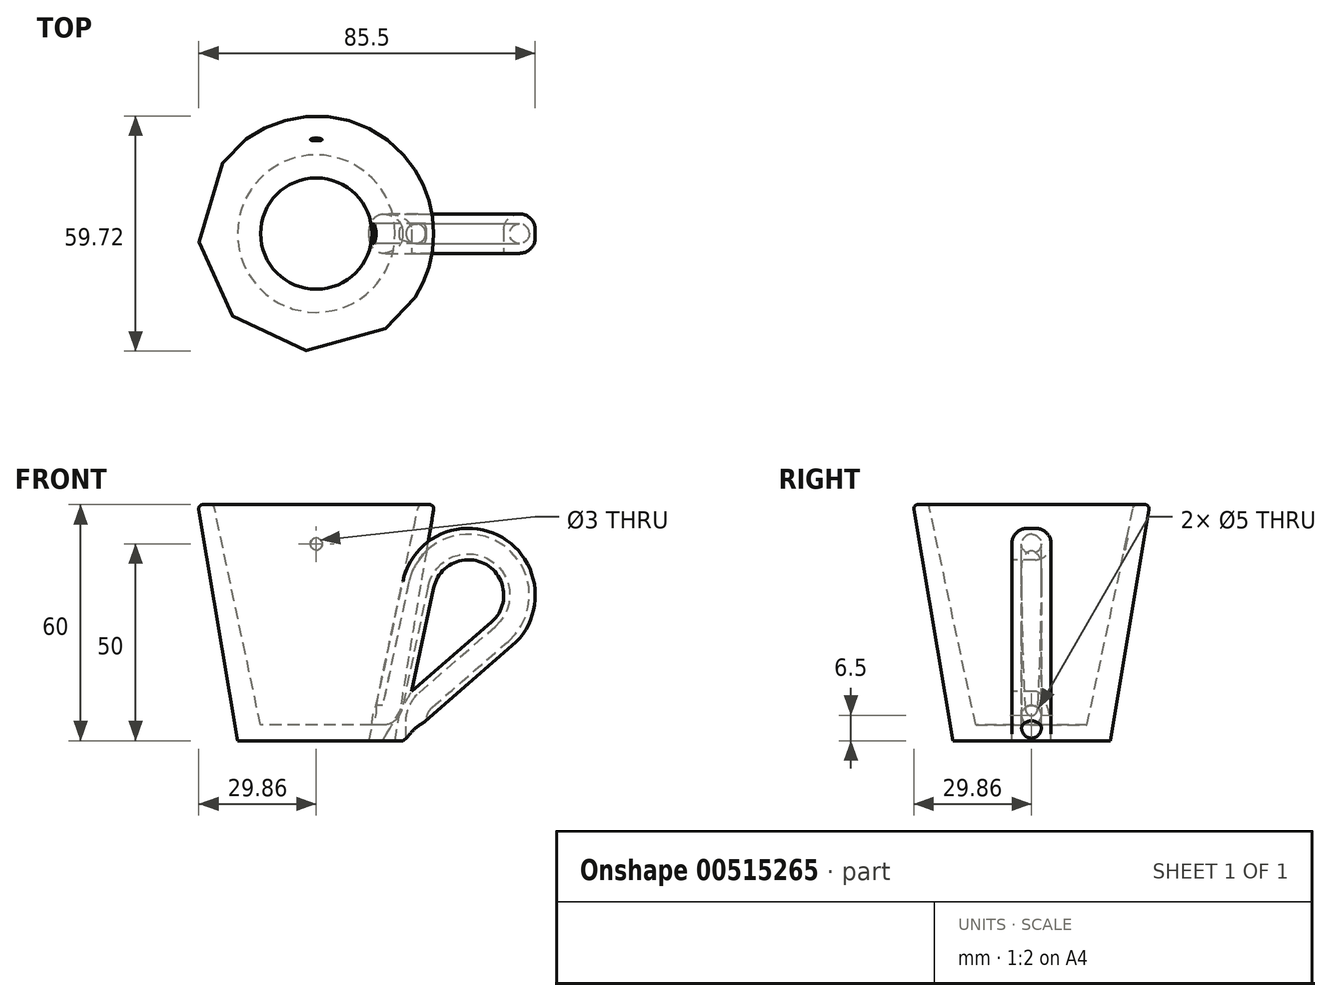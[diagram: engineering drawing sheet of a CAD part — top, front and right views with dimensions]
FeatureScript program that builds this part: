
annotation { "Feature Type Name" : "Feature", "Feature Type Description" : "" }
export const myFeature = defineFeature(function(context is Context, id is Id, definition is map)
    precondition{}
    {
        {
            var Q0;
            Q0=qCreatedBy(makeId("Top.planeOp"),FACE);
            var sketch = newSketch(context, id + "F0", { "sketchPlane" : qUnion([Q0])});
            skCircle(sketch, "E0", {"center": v(0, 0) * mm, "radius": 20 * mm});
            skSolve(sketch);
        }
        {
            var Q0;
            Q0 = qSketchRegion(id + "F0", true);
            extrude(context, id + "F1", {"entities" : qUnion([Q0]), "depth" : 60 * mm, "offsetDistance" : 25 * mm, "hasDraft" : true, "draftAngle" : 9.5 * degree});
        }
        {
            var Q0;
            Q0=makeQuery(id+"F1.opExtrude","CAP_FACE",FACE,{"disambiguationData":[OSD([sQuery(id+"F0.wireOp",EDGE,"E0")])],"isStart":false});
            var sketch = newSketch(context, id + "F2", { "sketchPlane" : qUnion([Q0])});
            skCircle(sketch, "E1.0", {"center": v(0, 0) * mm, "radius": 26.04 * mm});
            skSolve(sketch);
        }
        {
            var Q0;
            Q0 = qSketchRegion(id + "F2", true);
            extrude(context, id + "F3", {"entities" : qUnion([Q0]), "operationType" : NewBodyOperationType.REMOVE, "oppositeDirection" : true, "depth" : 56 * mm, "offsetDistance" : 25 * mm, "hasDraft" : true, "draftAngle" : 12 * degree, "draftPullDirection" : true});
        }
        {
            var Q0;
            Q0=qCreatedBy(makeId("Front.planeOp"),FACE);
            var sketch = newSketch(context, id + "F4", { "sketchPlane" : qUnion([Q0])});
            skLineSegment(sketch, "E2", {"start": v(13.4, 0) * mm, "end": v(22, 0) * mm});
            skLineSegment(sketch, "E3", {"start": v(22, 0) * mm, "end": v(49.8, 24.17) * mm});
            skArc(sketch, "E4", {"start": v(49.8, 24.17) * mm, "mid": v(47.27, 51.65) * mm, "end": v(22.02, 40.53) * mm});
            skLineSegment(sketch, "E5", {"start": v(13.4, 0) * mm, "end": v(22.02, 40.53) * mm});
            skSolve(sketch);
        }
        {
            var Q0;
            Q0 = qSketchRegion(id + "F4", true);
            extrude(context, id + "F5", {"entities" : qUnion([Q0]), "endBound" : BoundingType.SYMMETRIC, "depth" : 10 * mm, "offsetDistance" : 25 * mm});
        }
        {
            var Q0;
            Q0=makeQuery(id+"F5.opExtrude","CAP_FACE",FACE,{"disambiguationData":[OSD([sQuery(id+"F4.wireOp",EDGE,"E2"),sQuery(id+"F4.wireOp",EDGE,"E3"),sQuery(id+"F4.wireOp",EDGE,"E4"),sQuery(id+"F4.wireOp",EDGE,"E5")])],"isStart":false});
            var sketch = newSketch(context, id + "F6", { "sketchPlane" : qUnion([Q0])});
            skLineSegment(sketch, "E6.0", {"start": v(29.84, 38.87) * mm, "end": v(24.25, 12.56) * mm});
            skArc(sketch, "E6.1", {"start": v(44.55, 30.2) * mm, "mid": v(43.21, 44.75) * mm, "end": v(29.84, 38.87) * mm});
            skLineSegment(sketch, "E6.2", {"start": v(24.25, 12.56) * mm, "end": v(44.55, 30.2) * mm});
            skSolve(sketch);
        }
        {
            var Q0;
            Q0 = qSketchRegion(id + "F6", true);
            extrude(context, id + "F7", {"entities" : qUnion([Q0]), "operationType" : NewBodyOperationType.REMOVE, "endBound" : BoundingType.THROUGH_ALL, "oppositeDirection" : true, "depth" : 25 * mm, "offsetDistance" : 25 * mm});
        }
        {
            var Q0;
            Q0=makeQuery(id+"F7.boolean.opBoolean","COPY",EDGE,{"derivedFrom":makeQuery(id+"F7.opExtrude","CAP_EDGE",EDGE,{"disambiguationData":[OSD([sQuery(id+"F6.wireOp",EDGE,"E6.2")])],"isStart":true})});
            var Q1;
            Q1=makeQuery(id+"F7.boolean.opBoolean","INTERSECT",EDGE,{"derivedFrom":[makeQuery(id+"F5.opExtrude","CAP_FACE",FACE,{"disambiguationData":[OSD([sQuery(id+"F4.wireOp",EDGE,"E2"),sQuery(id+"F4.wireOp",EDGE,"E3"),sQuery(id+"F4.wireOp",EDGE,"E4"),sQuery(id+"F4.wireOp",EDGE,"E5")])],"isStart":true}),makeQuery(id+"F7.opExtrude","SWEPT_FACE",FACE,{"disambiguationData":[OSD([sQuery(id+"F6.wireOp",EDGE,"E6.2")])]})]});
            fillet(context, id + "F8", {"entities" : qUnion([Q0, Q1]), "radius" : 4 * mm, "tangentPropagation" : true, "allowEdgeOverflow" : false});
        }
        {
            var Q0;
            Q0=qCreatedBy(makeId("Front.planeOp"),FACE);
            var sketch = newSketch(context, id + "F9", { "sketchPlane" : qUnion([Q0])});
            skLineSegment(sketch, "E7", {"start": v(15.78, 4) * mm, "end": v(23.48, 40.22) * mm, "construction": true});
            skArc(sketch, "E8.0", {"start": v(48.81, 25.3) * mm, "mid": v(46.51, 50.36) * mm, "end": v(23.48, 40.22) * mm, "construction": true});
            skArc(sketch, "E9.0", {"start": v(45.53, 29.08) * mm, "mid": v(43.97, 46.05) * mm, "end": v(28.37, 39.18) * mm});
            skLineSegment(sketch, "E10", {"start": v(15.78, 4) * mm, "end": v(1.13, 4) * mm, "construction": true});
            skLineSegment(sketch, "E11", {"start": v(28.37, 39.18) * mm, "end": v(21.74, 7.96) * mm});
            skArc(sketch, "E12", {"start": v(16.85, 4) * mm, "mid": v(20, 5.11) * mm, "end": v(21.74, 7.96) * mm});
            skLineSegment(sketch, "E13", {"start": v(45.53, 29.08) * mm, "end": v(26.16, 12.23) * mm});
            skLineSegment(sketch, "E14", {"start": v(48.81, 25.3) * mm, "end": v(22.84, 2.72) * mm, "construction": true});
            skLineSegment(sketch, "E15.0", {"start": v(25.32, 4.9) * mm, "end": v(25.32, 0) * mm});
            skArc(sketch, "E15.1", {"start": v(27.8, 10.34) * mm, "mid": v(25.97, 7.9) * mm, "end": v(25.32, 4.9) * mm});
            skArc(sketch, "E15.2", {"start": v(16.85, 6.5) * mm, "mid": v(18.42, 7.06) * mm, "end": v(19.3, 8.48) * mm});
            skLineSegment(sketch, "E15.3", {"start": v(25.93, 39.7) * mm, "end": v(19.3, 8.48) * mm});
            skArc(sketch, "E15.4", {"start": v(47.17, 27.19) * mm, "mid": v(45.24, 48.2) * mm, "end": v(25.93, 39.7) * mm});
            skLineSegment(sketch, "E15.5", {"start": v(47.17, 27.19) * mm, "end": v(27.8, 10.34) * mm});
            skLineSegment(sketch, "E16", {"start": v(15.78, 4) * mm, "end": v(16.85, 4) * mm});
            skLineSegment(sketch, "E17", {"start": v(16.85, 6.5) * mm, "end": v(12.53, 6.5) * mm});
            skLineSegment(sketch, "E18", {"start": v(22.82, -3.18) * mm, "end": v(22.82, 4.9) * mm});
            skArc(sketch, "E19", {"start": v(26.16, 12.23) * mm, "mid": v(23.7, 8.93) * mm, "end": v(22.82, 4.9) * mm});
            skSolve(sketch);
        }
        {
            var Q0;
            Q0=qCreatedBy(makeId("Top.planeOp"),FACE);
            var sketch = newSketch(context, id + "F10", { "sketchPlane" : qUnion([Q0])});
            skCircle(sketch, "E20", {"center": v(25.32, 0) * mm, "radius": 2.5 * mm});
            skSolve(sketch);
        }
        {
            var Q0;
            Q0=makeQuery(id+"F10.imprint","IMPRINT",FACE,{"disambiguationData":[TD([[makeQuery(id+"F10.imprint","IMPRINT",EDGE,{"derivedFrom":sQuery(id+"F10.wireOp",EDGE,"E20")}),1.0]])]});
            var Q1;
            Q1=sQuery(id+"F9.wireOp",EDGE,"E15.0");
            var Q2;
            Q2=sQuery(id+"F9.wireOp",EDGE,"E15.1");
            var Q3;
            Q3=sQuery(id+"F9.wireOp",EDGE,"E15.5");
            var Q4;
            Q4=sQuery(id+"F9.wireOp",EDGE,"E15.4");
            var Q5;
            Q5=sQuery(id+"F9.wireOp",EDGE,"E15.3");
            var Q6;
            Q6=sQuery(id+"F9.wireOp",EDGE,"E15.2");
            var Q7;
            Q7=sQuery(id+"F9.wireOp",EDGE,"E17");
            sweep(context, id + "F11", {"operationType" : NewBodyOperationType.REMOVE, "profiles" : qUnion([Q0]), "path" : qUnion([Q1, Q2, Q3, Q4, Q5, Q6, Q7])});
        }
        {
            var Q0;
            Q0=makeQuery(id+"F5.opExtrude","CAP_EDGE",EDGE,{"disambiguationData":[OSD([sQuery(id+"F4.wireOp",EDGE,"E4")])],"isStart":false});
            var Q1;
            Q1=makeQuery(id+"F5.opExtrude","CAP_EDGE",EDGE,{"disambiguationData":[OSD([sQuery(id+"F4.wireOp",EDGE,"E4")])],"isStart":true});
            fillet(context, id + "F12", {"entities" : qUnion([Q0, Q1]), "radius" : 4 * mm, "tangentPropagation" : true, "allowEdgeOverflow" : false});
        }
        {
            var Q0;
            Q0=makeQuery(id+"F1.opExtrude","CAP_FACE",FACE,{"disambiguationData":[OSD([sQuery(id+"F0.wireOp",EDGE,"E0")])],"isStart":false});
            fillet(context, id + "F13", {"entities" : qUnion([Q0]), "radius" : 1 * mm, "tangentPropagation" : true, "allowEdgeOverflow" : false});
        }
        {
            var Q0;
            Q0=qCreatedBy(makeId("Front.planeOp"),FACE);
            var sketch = newSketch(context, id + "F14", { "sketchPlane" : qUnion([Q0])});
            skCircle(sketch, "E21", {"center": v(0, 50) * mm, "radius": 1.5 * mm});
            skSolve(sketch);
        }
        {
            var Q0;
            Q0 = qSketchRegion(id + "F14", true);
            var Q1;
            Q1=makeQuery(id+"F3.boolean.opBoolean","COPY",FACE,{"derivedFrom":makeQuery(id+"F3.opExtrude","SWEPT_FACE",FACE,{"disambiguationData":[OSD([sQuery(id+"F2.wireOp",EDGE,"E1.0")])]})});
            extrude(context, id + "F15", {"entities" : qUnion([Q0]), "operationType" : NewBodyOperationType.REMOVE, "endBound" : BoundingType.UP_TO_SURFACE, "oppositeDirection" : true, "depth" : 25 * mm, "endBoundEntityFace" : qUnion([Q1]), "hasOffset" : true, "offsetDistance" : -0.2 * mm});
        }
    });
